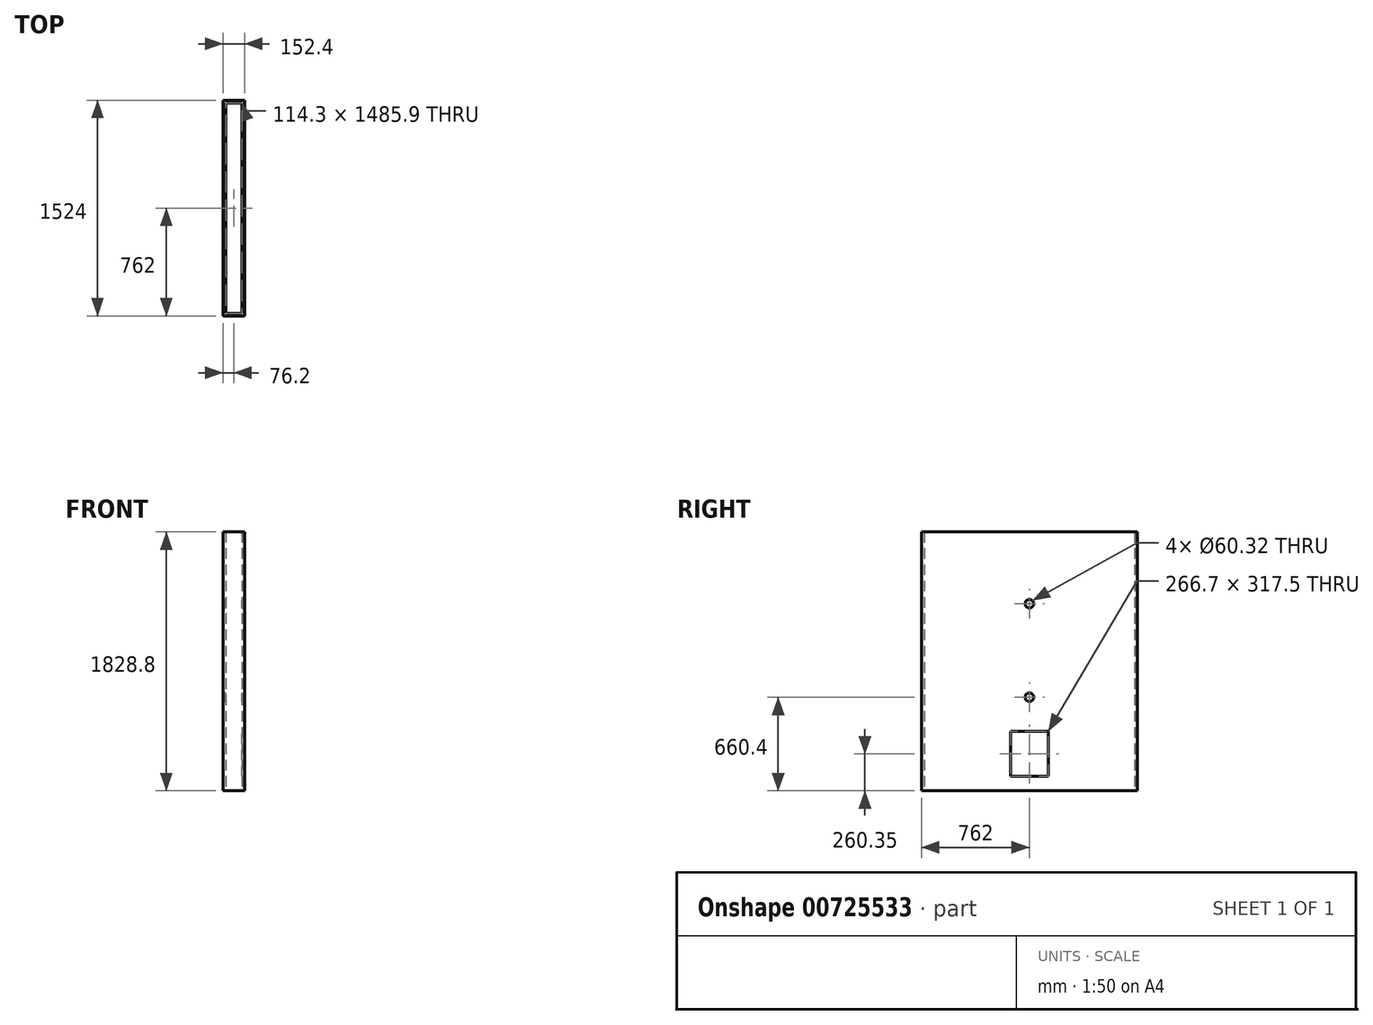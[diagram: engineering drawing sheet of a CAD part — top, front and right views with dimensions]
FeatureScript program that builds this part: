
annotation { "Feature Type Name" : "Feature", "Feature Type Description" : "" }
export const myFeature = defineFeature(function(context is Context, id is Id, definition is map)
    precondition{}
    {
        {
            var Q0;
            Q0=qCreatedBy(makeId("Top.planeOp"),FACE);
            var sketch = newSketch(context, id + "F0", { "sketchPlane" : qUnion([Q0])});
            skLineSegment(sketch, "E0.bottom", {"start": v(-76.2, 762) * mm, "end": v(76.2, 762) * mm});
            skLineSegment(sketch, "E0.top", {"start": v(-76.2, -762) * mm, "end": v(76.2, -762) * mm});
            skLineSegment(sketch, "E0.left", {"start": v(-76.2, 762) * mm, "end": v(-76.2, -762) * mm});
            skLineSegment(sketch, "E0.right", {"start": v(76.2, 762) * mm, "end": v(76.2, -762) * mm});
            skPoint(sketch, "E0.middle", {"position": v(0, 0) * mm});
            skLineSegment(sketch, "E1.bottom", {"start": v(57.15, 742.95) * mm, "end": v(-57.15, 742.95) * mm});
            skLineSegment(sketch, "E1.top", {"start": v(57.15, -742.95) * mm, "end": v(-57.15, -742.95) * mm});
            skLineSegment(sketch, "E1.left", {"start": v(57.15, 742.95) * mm, "end": v(57.15, -742.95) * mm});
            skLineSegment(sketch, "E1.right", {"start": v(-57.15, 742.95) * mm, "end": v(-57.15, -742.95) * mm});
            skSolve(sketch);
        }
        {
            var Q0;
            Q0=makeQuery(id+"F0.imprint","IMPRINT",FACE,{"disambiguationData":[TD([[makeQuery(id+"F0.imprint","IMPRINT",EDGE,{"derivedFrom":sQuery(id+"F0.wireOp",EDGE,"E0.bottom")}),-1.0]])]});
            extrude(context, id + "F1", {"entities" : qUnion([Q0]), "depth" : 1828.8 * mm, "offsetDistance" : 25.4 * mm});
        }
        {
            var Q0;
            Q0=makeQuery(id+"F1.opExtrude","SWEPT_FACE",FACE,{"disambiguationData":[OSD([sQuery(id+"F0.wireOp",EDGE,"E0.right")])]});
            var sketch = newSketch(context, id + "F2", { "sketchPlane" : qUnion([Q0])});
            skLineSegment(sketch, "E2", {"start": v(0, 1828.8) * mm, "end": v(0, 1320.8) * mm});
            skLineSegment(sketch, "E3", {"start": v(0, 0) * mm, "end": v(0, 660.4) * mm});
            skCircle(sketch, "E4", {"center": v(0, 1320.8) * mm, "radius": 30.16 * mm});
            skCircle(sketch, "E5", {"center": v(0, 660.4) * mm, "radius": 30.16 * mm});
            skLineSegment(sketch, "E6", {"start": v(0, 0) * mm, "end": v(0, 260.35) * mm});
            skLineSegment(sketch, "E7.bottom", {"start": v(133.35, 101.6) * mm, "end": v(-133.35, 101.6) * mm});
            skLineSegment(sketch, "E7.top", {"start": v(133.35, 419.1) * mm, "end": v(-133.35, 419.1) * mm});
            skLineSegment(sketch, "E7.left", {"start": v(133.35, 101.6) * mm, "end": v(133.35, 419.1) * mm});
            skLineSegment(sketch, "E7.right", {"start": v(-133.35, 101.6) * mm, "end": v(-133.35, 419.1) * mm});
            skPoint(sketch, "E7.middle", {"position": v(0, 260.35) * mm});
            skSolve(sketch);
        }
        {
            var Q0;
            {var subQ0=sQuery(id+"F2.wireOp",EDGE,"E7.right");Q0=makeQuery(id+"F2.imprint","IMPRINT",FACE,{"disambiguationData":[TD([[makeQuery(id+"F2.imprint","IMPRINT",EDGE,{"derivedFrom":subQ0}),-1.0]])]});}
            var Q1;
            {var subQ0=sQuery(id+"F2.wireOp",EDGE,"E7.left");Q1=makeQuery(id+"F2.imprint","IMPRINT",FACE,{"disambiguationData":[TD([[makeQuery(id+"F2.imprint","IMPRINT",EDGE,{"derivedFrom":subQ0}),1.0]])]});}
            var Q2;
            Q2=makeQuery(id+"F2.imprint","IMPRINT",FACE,{"disambiguationData":[TD([[makeQuery(id+"F2.imprint","IMPRINT",EDGE,{"derivedFrom":sQuery(id+"F2.wireOp",EDGE,"E5")}),1.0]])]});
            var Q3;
            Q3=makeQuery(id+"F2.imprint","IMPRINT",FACE,{"disambiguationData":[TD([[makeQuery(id+"F2.imprint","IMPRINT",EDGE,{"derivedFrom":sQuery(id+"F2.wireOp",EDGE,"E4")}),1.0]])]});
            extrude(context, id + "F3", {"entities" : qUnion([Q0, Q1, Q2, Q3]), "operationType" : NewBodyOperationType.REMOVE, "oppositeDirection" : true, "depth" : 25.4 * mm, "offsetDistance" : 25.4 * mm});
        }
        {
            var Q0;
            Q0=makeQuery(id+"F1.opExtrude","SWEPT_FACE",FACE,{"disambiguationData":[OSD([sQuery(id+"F0.wireOp",EDGE,"E0.left")])]});
            var sketch = newSketch(context, id + "F4", { "sketchPlane" : qUnion([Q0])});
            skLineSegment(sketch, "E8", {"start": v(0, 1828.8) * mm, "end": v(0, 1320.8) * mm});
            skLineSegment(sketch, "E9", {"start": v(0, 0) * mm, "end": v(0, 660.4) * mm});
            skCircle(sketch, "E10", {"center": v(0, 1320.8) * mm, "radius": 30.16 * mm});
            skCircle(sketch, "E11", {"center": v(0, 660.4) * mm, "radius": 30.16 * mm});
            skSolve(sketch);
        }
        {
            var Q0;
            Q0=makeQuery(id+"F4.imprint","IMPRINT",FACE,{"disambiguationData":[TD([[makeQuery(id+"F4.imprint","IMPRINT",EDGE,{"derivedFrom":sQuery(id+"F4.wireOp",EDGE,"E10")}),1.0]])]});
            var Q1;
            Q1=makeQuery(id+"F4.imprint","IMPRINT",FACE,{"disambiguationData":[TD([[makeQuery(id+"F4.imprint","IMPRINT",EDGE,{"derivedFrom":sQuery(id+"F4.wireOp",EDGE,"E11")}),1.0]])]});
            extrude(context, id + "F5", {"entities" : qUnion([Q0, Q1]), "operationType" : NewBodyOperationType.REMOVE, "oppositeDirection" : true, "depth" : 25.4 * mm, "offsetDistance" : 25.4 * mm});
        }
    });
